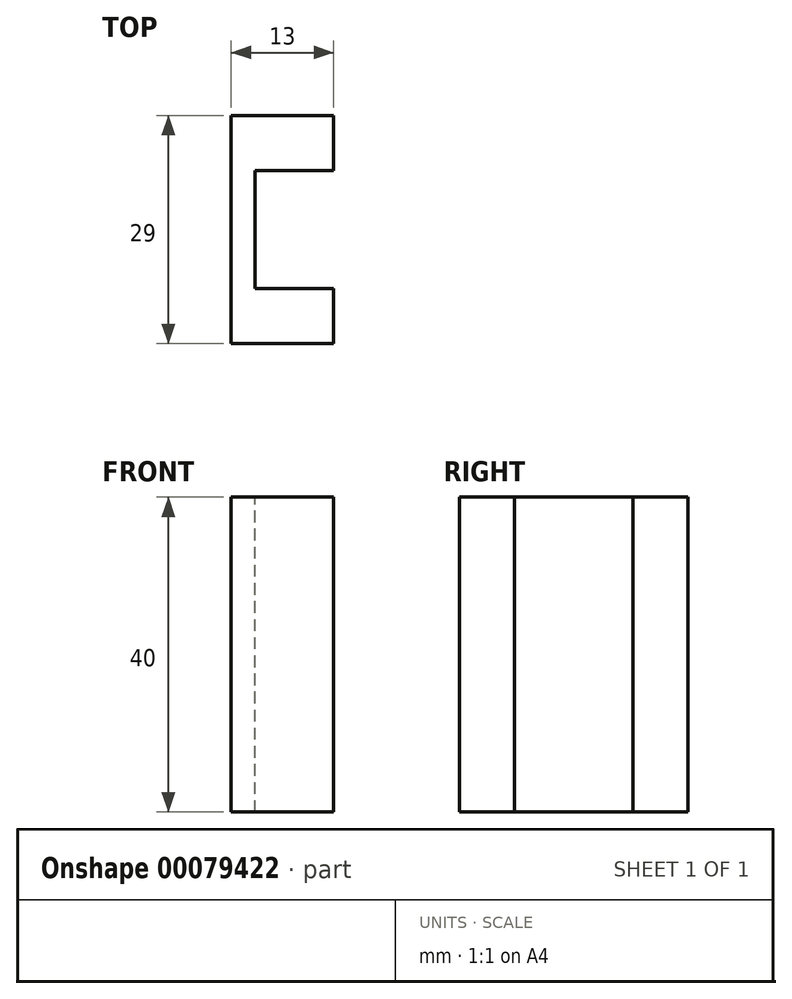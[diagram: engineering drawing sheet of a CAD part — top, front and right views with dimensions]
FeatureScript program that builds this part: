
annotation { "Feature Type Name" : "Feature", "Feature Type Description" : "" }
export const myFeature = defineFeature(function(context is Context, id is Id, definition is map)
    precondition{}
    {
        {
            var Q0;
            Q0=qCreatedBy(makeId("Top.planeOp"),FACE);
            var sketch = newSketch(context, id + "F0", { "sketchPlane" : qUnion([Q0])});
            skLineSegment(sketch, "E0.bottom", {"start": v(-9.49, 5.13) * mm, "end": v(3.51, 5.13) * mm});
            skLineSegment(sketch, "E0.top", {"start": v(-9.49, -1.87) * mm, "end": v(3.51, -1.87) * mm});
            skLineSegment(sketch, "E0.left", {"start": v(-9.49, 5.13) * mm, "end": v(-9.49, -1.87) * mm});
            skLineSegment(sketch, "E0.right", {"start": v(3.51, 5.13) * mm, "end": v(3.51, -1.87) * mm});
            skSolve(sketch);
        }
        {
            var Q0;
            Q0=makeQuery(id+"F0.imprint","IMPRINT",FACE,{"disambiguationData":[TD([[makeQuery(id+"F0.imprint","IMPRINT",EDGE,{"derivedFrom":sQuery(id+"F0.wireOp",EDGE,"E0.bottom")}),-1.0]])]});
            extrude(context, id + "F1", {"entities" : qUnion([Q0]), "depth" : 40 * mm});
        }
        {
            var Q0;
            Q0=makeQuery(id+"F1.opExtrude","SWEPT_FACE",FACE,{"disambiguationData":[OSD([sQuery(id+"F0.wireOp",EDGE,"E0.left")])]});
            var sketch = newSketch(context, id + "F2", { "sketchPlane" : qUnion([Q0])});
            skLineSegment(sketch, "E1.bottom", {"start": v(1.87, 40) * mm, "end": v(-20.13, 40) * mm});
            skLineSegment(sketch, "E1.top", {"start": v(1.87, 0) * mm, "end": v(-20.13, 0) * mm});
            skLineSegment(sketch, "E1.left", {"start": v(1.87, 40) * mm, "end": v(1.87, 0) * mm});
            skLineSegment(sketch, "E1.right", {"start": v(-20.13, 40) * mm, "end": v(-20.13, 0) * mm});
            skSolve(sketch);
        }
        {
            var Q0;
            {var subQ2=sQuery(id+"F2.wireOp",EDGE,"E1.left");Q0=makeQuery(id+"F2.imprint","IMPRINT",FACE,{"disambiguationData":[TD([[makeQuery(id+"F2.imprint","IMPRINT",EDGE,{"derivedFrom":subQ2}),-1.0]])]});}
            var Q1;
            {var subQ2=sQuery(id+"F2.wireOp",EDGE,"E1.right");Q1=makeQuery(id+"F2.imprint","IMPRINT",FACE,{"disambiguationData":[TD([[makeQuery(id+"F2.imprint","IMPRINT",EDGE,{"derivedFrom":subQ2}),1.0]])]});}
            extrude(context, id + "F3", {"entities" : qUnion([Q0, Q1]), "operationType" : NewBodyOperationType.ADD, "oppositeDirection" : true, "depth" : 3 * mm});
        }
        {
            var Q0;
            Q0=makeQuery(id+"F3.opExtrude","SWEPT_FACE",FACE,{"disambiguationData":[OSD([sQuery(id+"F2.wireOp",EDGE,"E1.right")])]});
            var sketch = newSketch(context, id + "F4", { "sketchPlane" : qUnion([Q0])});
            skLineSegment(sketch, "E2.bottom", {"start": v(9.49, 40) * mm, "end": v(-3.51, 40) * mm});
            skLineSegment(sketch, "E2.top", {"start": v(9.49, 0) * mm, "end": v(-3.51, 0) * mm});
            skLineSegment(sketch, "E2.left", {"start": v(9.49, 40) * mm, "end": v(9.49, 0) * mm});
            skLineSegment(sketch, "E2.right", {"start": v(-3.51, 40) * mm, "end": v(-3.51, 0) * mm});
            skSolve(sketch);
        }
        {
            var Q0;
            Q0 = qSketchRegion(id + "F4", true);
            extrude(context, id + "F5", {"entities" : qUnion([Q0]), "operationType" : NewBodyOperationType.ADD, "depth" : 7 * mm});
        }
    });
